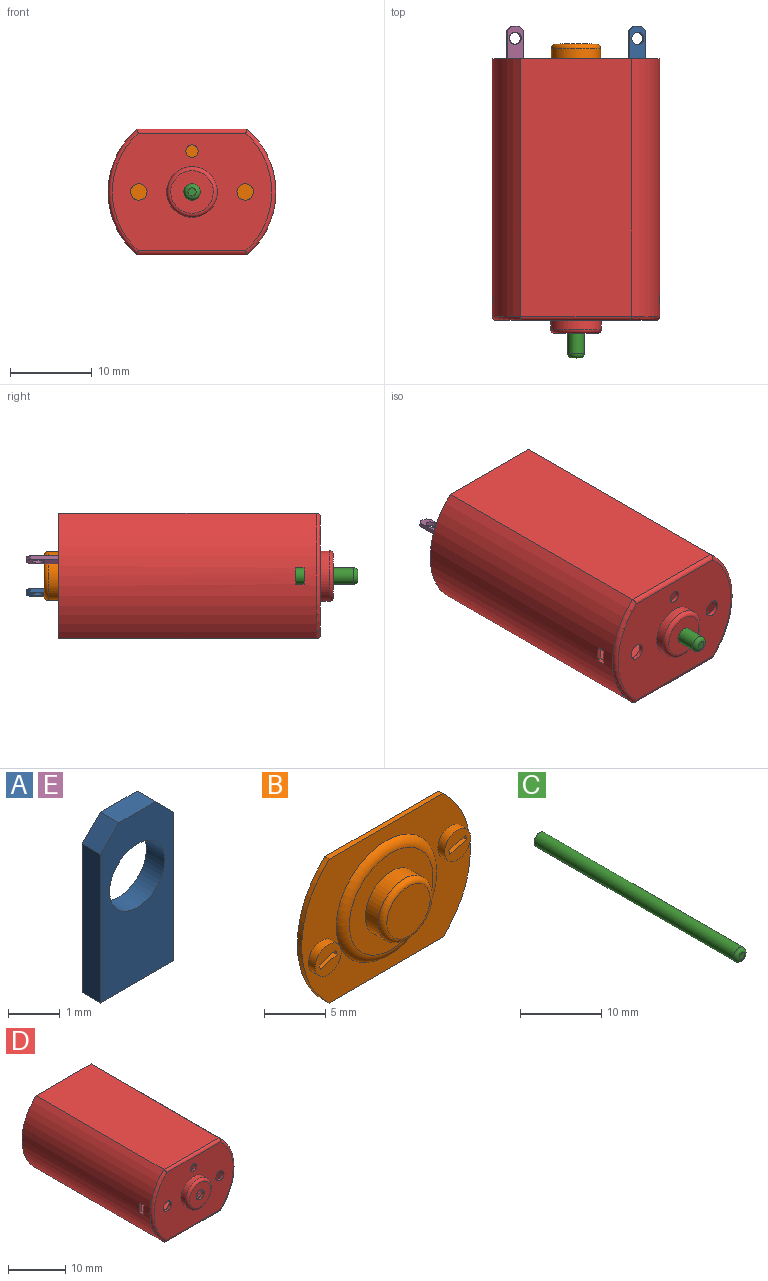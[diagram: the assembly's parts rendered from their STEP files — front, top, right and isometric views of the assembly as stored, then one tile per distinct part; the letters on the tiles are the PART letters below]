
ASSEMBLY  parts=5 mates=8
PART A: 9 faces, bbox 2x0.5x4 mm
  f0: plane 3.5x0.5mm, normal (1,0,0), area 1.8mm2, adj f3,f5,f6,f8
  f1: plane 1x0.5mm, normal (0,0,1), area 0.5mm2, adj f5,f6,f7,f8
  f2: plane 3.5x0.5mm, normal (-1,0,0), area 1.8mm2, adj f3,f5,f6,f7
  f3: plane 2x0.5mm, normal (0,0,-1), area 1mm2, adj f0,f2,f5,f6
  f4: cylinder r=0.75mm len=1.5mm, axis (0,1,0), area 2.4mm2, adj f5,f6
  f5: plane 4x2mm, normal (0,-1,0), area 6mm2, adj f0,f1,f2,f3,f4,f7,f8
  f6: plane 4x2mm, normal (0,1,0), area 6mm2, adj f0,f1,f2,f3,f4,f7,f8
  f7: plane 0.5x0.5mm, normal (-0.71,0,0.71), area 0.4mm2, adj f1,f2,f5,f6
  f8: plane 0.5x0.5mm, normal (0.71,0,0.71), area 0.4mm2, adj f0,f1,f5,f6
PART B: 25 faces, bbox 19.5x3.1x14.4 mm
  f0: plane 19.5x14.4mm, normal (0,-1,0), area 134.6mm2, adj f1,f2,f3,f4,f7,f14,f22
  f1: plane 13.15x0.5mm, normal (0,0,-1), area 6.6mm2, adj f0,f2,f4,f5
  f2: cylinder r=9.75mm len=14.4mm, axis (0,1,0), area 8.1mm2, adj f0,f1,f3,f5
  f3: plane 13.15x0.5mm, normal (0,0,1), area 6.6mm2, adj f0,f2,f4,f5
  f4: cylinder r=9.75mm len=14.4mm, axis (0,1,0), area 8.1mm2, adj f0,f1,f3,f5
  f5: plane 19.5x14.4mm, normal (0,1,0), area 252.6mm2, adj f1,f2,f3,f4
  f6: plane 9.67x9.67mm, normal (0,-1,0), area 45.1mm2, adj f7,f8
  f7: torus R=4.83mm, axis (0,1,0), area 39mm2, adj f0,f6
  f8: cylinder r=3mm len=6mm, axis (0,1,0), area 28.3mm2, adj f6,f10
  f9: plane 5x5mm, normal (0,-1,0), area 19.6mm2, adj f10
  f10: torus R=2.5mm, axis (0,-1,0), area 13.9mm2, adj f8,f9
  f11: plane 0.8x0.48mm, normal (0.97,0,0.26), area 0.4mm2, adj f12,f15,f16,f17
  f12: plane 1.93x0.8mm, normal (0.26,0,-0.97), area 1.6mm2, adj f11,f13,f16,f17
  f13: plane 0.8x0.48mm, normal (-0.97,0,-0.26), area 0.4mm2, adj f12,f15,f16,f17
  f14: cylinder r=1.5mm len=3mm, axis (0,1,0), area 7.5mm2, adj f0,f16
  f15: plane 1.93x0.8mm, normal (-0.26,0,0.97), area 1.6mm2, adj f11,f13,f16,f17
  f16: plane 3x3mm, normal (0,-1,0), area 6.1mm2, adj f11,f12,f13,f14,f15
  f17: plane 2.06x1mm, normal (0,-1,0), area 1mm2, adj f11,f12,f13,f15
  f18: plane 1.93x0.8mm, normal (0.26,0,-0.97), area 1.6mm2, adj f19,f21,f23,f24
  f19: plane 0.8x0.48mm, normal (-0.97,0,-0.26), area 0.4mm2, adj f18,f20,f23,f24
  f20: plane 1.93x0.8mm, normal (-0.26,0,0.97), area 1.6mm2, adj f19,f21,f23,f24
  f21: plane 0.8x0.48mm, normal (0.97,0,0.26), area 0.4mm2, adj f18,f20,f23,f24
  f22: cylinder r=1.5mm len=3mm, axis (0,1,0), area 7.5mm2, adj f0,f23
  f23: plane 3x3mm, normal (0,-1,0), area 6.1mm2, adj f18,f19,f20,f21,f22
  f24: plane 2.06x1mm, normal (0,-1,0), area 1mm2, adj f18,f19,f20,f21
PART C: 4 faces, bbox 2.2x35.3x2.2 mm
  f0: cylinder r=1mm len=34.8mm, axis (0,1,0), area 218.7mm2, adj f2,f3
  f1: plane 1x1mm, normal (0,-1,0), area 0.8mm2, adj f3
  f2: plane 2x2mm, normal (0,1,0), area 3.1mm2, adj f0
  f3: torus R=0.5mm, axis (0,-1,0), area 4mm2, adj f0,f1
PART D: 32 faces, bbox 22.2x33.6x16.7 mm
  f0: cylinder r=10.25mm len=31.5mm, axis (0,1,0), area 546.8mm2, adj f4,f5,f6,f21,f28,f29,f30,f31
  f1: cylinder r=10.25mm len=31.5mm, axis (0,1,0), area 546.8mm2, adj f4,f5,f6,f22,f24,f25,f26,f27
  f2: cylinder r=9.75mm len=31.5mm, axis (0,1,0), area 508.3mm2, adj f4,f10,f11,f12,f28,f29,f30,f31
  f3: cylinder r=9.75mm len=31.5mm, axis (0,1,0), area 508.3mm2, adj f4,f10,f11,f12,f24,f25,f26,f27
  f4: plane 20.5x15.4mm, normal (0,1,0), area 30.2mm2, adj f0,f1,f2,f3,f5,f6,f10,f11
  f5: plane 31.5x13.53mm, normal (0,0,1), area 426.2mm2, adj f0,f1,f4,f20
  f6: plane 31.5x13.53mm, normal (0,0,-1), area 426.2mm2, adj f0,f1,f4,f23
  f7: plane 19.5x14.4mm, normal (0,-1,0), area 214.4mm2, adj f8,f16,f17,f18,f20,f21,f22,f23
  f8: cylinder r=3.1mm len=6.2mm, axis (0,1,0), area 21.4mm2, adj f7,f19
  f9: plane 5.2x5.2mm, normal (0,-1,0), area 18.1mm2, adj f15,f19
  f10: plane 31.5x13.15mm, normal (0,0,-1), area 414.2mm2, adj f2,f3,f4,f12
  f11: plane 31.5x13.15mm, normal (0,0,1), area 414.2mm2, adj f2,f3,f4,f12
  f12: plane 19.5x14.4mm, normal (0,1,0), area 223.3mm2, adj f2,f3,f10,f11,f13,f16,f17,f18
  f13: cylinder r=2.6mm len=5.2mm, axis (0,1,0), area 26.1mm2, adj f12,f14
  f14: plane 5.2x5.2mm, normal (0,1,0), area 18.1mm2, adj f13,f15
  f15: cylinder r=1mm len=2mm, axis (0,-1,0), area 3.1mm2, adj f9,f14
  f16: cylinder r=0.75mm len=1.5mm, axis (0,-1,0), area 2.4mm2, adj f7,f12
  f17: cylinder r=1mm len=2mm, axis (0,-1,0), area 3.1mm2, adj f7,f12
  f18: cylinder r=1mm len=2mm, axis (0,-1,0), area 3.1mm2, adj f7,f12
  f19: torus R=2.6mm, axis (0,-1,0), area 14.4mm2, adj f8,f9
  f20: cylinder r=0.5mm len=13.53mm, axis (1,0,0), area 10.5mm2, adj f5,f7,f21,f22
  f21: torus R=9.75mm, axis (0,-1,0), area 13.3mm2, adj f0,f7,f20,f23
  f22: torus R=9.75mm, axis (0,-1,0), area 13.3mm2, adj f1,f7,f20,f23
  f23: cylinder r=0.5mm len=13.53mm, axis (-1,0,0), area 10.5mm2, adj f6,f7,f21,f22
  f24: plane 2x0.55mm, normal (0,1,0), area 1mm2, adj f1,f3,f25,f27
  f25: plane 1x0.5mm, normal (0,0,-1), area 0.5mm2, adj f1,f3,f24,f26
  f26: plane 2x0.55mm, normal (0,-1,0), area 1mm2, adj f1,f3,f25,f27
  f27: plane 1x0.5mm, normal (0,0,1), area 0.5mm2, adj f1,f3,f24,f26
  f28: plane 1x0.5mm, normal (0,0,1), area 0.5mm2, adj f0,f2,f29,f31
  f29: plane 2x0.55mm, normal (0,-1,0), area 1mm2, adj f0,f2,f28,f30
  f30: plane 1x0.5mm, normal (0,0,-1), area 0.5mm2, adj f0,f2,f29,f31
  f31: plane 2x0.55mm, normal (0,1,0), area 1mm2, adj f0,f2,f28,f30
PART E: same geometry as A
PLACE A rot(axis=(-0.98,0.13,0.13),91deg) t=(7.42,2,-2.25)mm
PLACE B rot(axis=(-1,0,0),180deg) t=(0,-1.3,0)mm
PLACE C rot(axis=(0,1,0),13.6deg) t=(0,-1.3,0)mm
PLACE D at identity fixed
PLACE E rot(axis=(-0.98,0.13,0.13),91deg) t=(-7.55,2,1.76)mm
MATE planar B.f22 <-> A.f3  axis (0,1,0) through (7.49,0,-2.01)mm
MATE planar B.f11 <-> E.f2  axis (0.97,0,-0.26) through (-8.45,-0.4,2.26)mm
MATE planar B.f21 <-> A.f2  axis (0.97,0,-0.26) through (6.52,-0.4,-1.75)mm
MATE cylindrical C.f0 <-> B.f8  axis (0,1,0) through (0,-1.3,0)mm
MATE planar E.f5 <-> B.f15  axis (0.26,0,0.97) through (-8.39,1.75,2.51)mm
MATE planar A.f6 <-> B.f18  axis (-0.26,0,-0.97) through (7.42,1.78,-2.25)mm
MATE slider D.f0 <-> B.f4  axis (0,1,0) through (0,0,0)mm
MATE planar B.f14 <-> E.f3  axis (0,1,0) through (-7.49,0,2.01)mm
